# Revit family: Masterwatt_CALIDA COMPACT DUO
name_source: partatom
category: Mechanical Equipment
revit_build: Autodesk Revit 2018 (Build: 20190510_1515(x64)
units: mm (PartAtom-declared; Revit-internal decimal feet)

## family parameters
Always vertical = Yes
Classification = None
Cut with Voids When Loaded = No
OmniClass Number = 23.75.10.11.14
OmniClass Title = Hot Water Heat Generators
Part Type = Normal
Room Calculation Point = No
Round Connector Dimension = Use Diameter
Shared = No
Work Plane-Based = No

## types (2) — shared parameters
Breedte = 580 mm  [stored 1.90289 ft]
Diepte = 630 mm  [stored 2.06693 ft]
Diepte aansluiting = 60 mm  [stored 0.19685 ft]
Hoogte = 1745 mm
Hoogte bedieningspaneel = 1300 mm  [stored 4.26509 ft]
Materiaal_01 = Coating wit
Materiaal_02 = Kunststof wit mat
Model = EKD.M3
URL = https://masterwatt.nl
Voltage = 230 V

## per-type parameters (varying)
| type | Art. No. | Watt |
| EKD.M3-04/06/08 | 300 100 108 | 4000 VA |
| EKD.M3-12/16/20/24 | 300 100 124 | 12000 VA |

note: [stored X ft] marks values corroborated as IEEE doubles in the binary element streams (Revit-internal decimal feet)

## geometry (parser evidence)
native form markers: Sweep x6
no freeform markers — native parametric forms only
